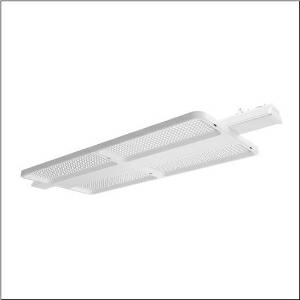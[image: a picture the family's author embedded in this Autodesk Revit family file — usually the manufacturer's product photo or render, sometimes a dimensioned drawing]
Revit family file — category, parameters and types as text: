
# Revit family: highbay_11_fur_licross_r__tragschiene_maxi_51hn12db4qla02_12de
name_source: partatom
category: Lighting Fixtures
units: mm (PartAtom-declared; Revit-internal decimal feet)

## family parameters
Cut with Voids When Loaded = No
Host = Face
Light Source = No
Part Type = Normal
Room Calculation Point = No
Round Connector Dimension = Use Diameter
Shared = No

## types (1)
- --- (1 x LED, 36000 lm, 178.2 W, 4000K)
    Apparent Load = 178 VA
    CIE Flux Codes = 87 98 100 100 100
    Color Rendering = 80
    Color Temperature = 4000K
    Default Elevation = 1800 mm
    Description = high bay luminaire Highbay 11 for Licross® trunking rail maxi; direct symmetric wide distribution, light control with lens of PMMA; UGR ≤ 22 (X = 4H | Y = 8H | S = 0.25H | reflection values 70/50/20); luminous flux: 36.000lm; light colour: 840, colour temperature: 4000K, MacAdam ≤ 2 SDCM (initial), colour rendering: CRI > 80; luminous efficacy: 202lm/W; rated service life: 100.000h (L95/B50) at AT= 25°C; control: Bluetooth® Mesh; for wireless networking: Node luminaire for setting up a local control solution without a higher-level application controller, intelligence completely in the luminaire; no control line such as DALI between the Node multi-sensor luminaires and Nodes is required, wireless integration of other Node luminaires and Node multi-sensor luminaires into the network is possible; number of Node luminaires in the project can be expanded as required, network sizes > 300 Nodes can be realized; can also be connected to lighting or building automation via various gateways upon request; integrated DALI2 ECG provides luminaire data (according to IEC62386, Part 251), energy data (Part 252), and monitoring and analytics data (Part 253) to higher-level systems for further processing; luminaire connection: plug, 5-pole, with phase selectionmains connection: 230..240V, AC 50/60Hz; connected load: 178,2W; protection rating (complete): IP64; insulation class (complete): insulation class I (protective earthing); protection symbol: D; impact resistance: IK07; certification: CE, ENEC, VDE, UKCA; internal wiring halogen-free; luminaire corresponds to IFS (International Featured Standards) requirements for safety and quality in the food industry; LABS conformity tested according to VDMA 24364:2018-05; housing frame of high-performance plastic PA6, matt traffic white (RAL 9016); cover of PMMA; fixing on rail side of steel, galvanised, white; blank cover of PC/ABS, traffic white (RAL 9016); dimension (LxWxH): 1.250 x 442 x 72mm; permissible operating ambient temperature: -20..+40°C (reducing of maximum allowable ambient temperature of 5°C with ceiling mounting); packaging unit: 1 piece
    Height = 72 mm  [stored 0.23622 ft]
    Lamp = 1 x LED
    Lamp Light Flux = 36000 lm
    Lamp Power = 178.2 W
    Lamp count = 1
    Length = 946 mm
    Luminous efficacy = 202 lm/W
    Manufacturer = Siteco
    ModVariant = No
    Model = 51HN12DB4QLA02
    Mounting Place = Ceiling
    Mounting Type = Pendant
    Number of Poles = 1
    OnlyDefault = Yes
    Power Factor = 1
    Product Name = Highbay 11 für Licross® Tragschiene maxi
    Product group = high bay luminaire
    ProductGroupID = 901
    Protection Class = Protection class I
    Protection Degree = IP 64
    RLX_Detail_Level = 1
    RLX_Emergency_Light_Flux = 0 lm
    RLX_Emergency_Type = 0
    RLX_Emergency_Type_DB = No
    RlxData = <blob elided: 25185 chars, md5=505e6165>
    Socket = socket
    Standby Power = 0 W
    System Light Flux = 36000 lm
    System Power = 178 W
    Type Comments = factory setting: luminous flux: 100 % | dim-lin: 254 | 824 mA
    Type Image = l_1361711.jpg
    URL = http://relux.com
    VarID = @adj_024565
    Voltage = 0 V
    Weight = 0.00 kg
    Width = 442 mm

note: [stored X ft] marks values corroborated as IEEE doubles in the binary element streams (Revit-internal decimal feet)

## geometry (parser evidence)
native form markers: Blend x4, Sweep x11
no freeform markers — native parametric forms only
